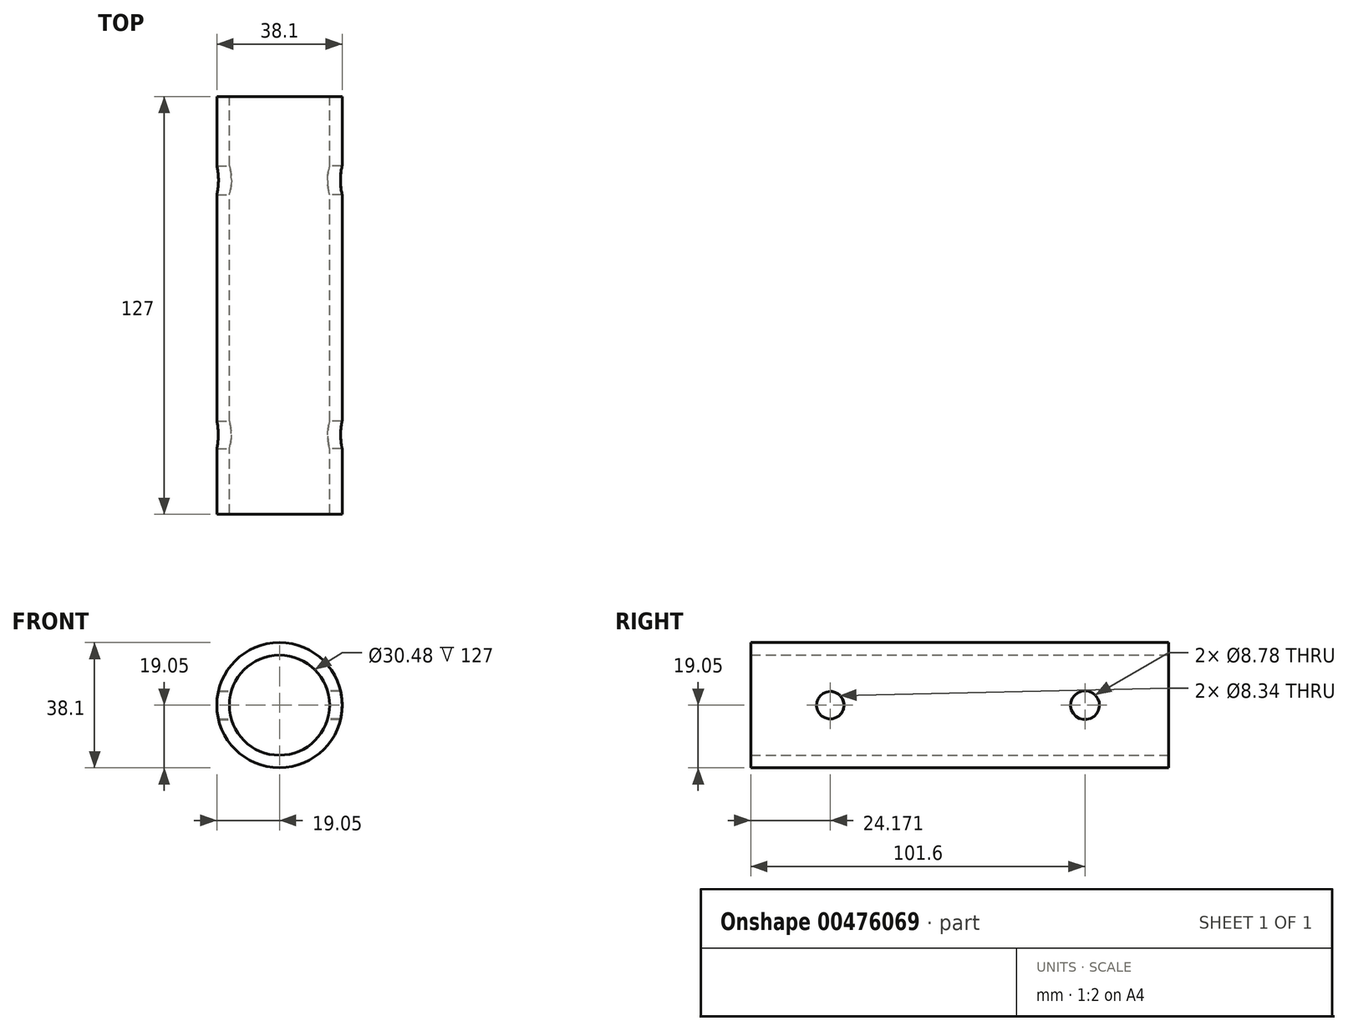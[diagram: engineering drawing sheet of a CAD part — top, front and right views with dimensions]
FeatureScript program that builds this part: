
annotation { "Feature Type Name" : "Feature", "Feature Type Description" : "" }
export const myFeature = defineFeature(function(context is Context, id is Id, definition is map)
    precondition{}
    {
        {
            var Q0;
            Q0=qCreatedBy(makeId("Front.planeOp"),FACE);
            var sketch = newSketch(context, id + "F0", { "sketchPlane" : qUnion([Q0])});
            skCircle(sketch, "E0", {"center": v(0, 0) * mm, "radius": 19.05 * mm});
            skSolve(sketch);
        }
        {
            var Q0;
            Q0=makeQuery(id+"F0.imprint","IMPRINT",FACE,{"disambiguationData":[TD([[makeQuery(id+"F0.imprint","IMPRINT",EDGE,{"derivedFrom":sQuery(id+"F0.wireOp",EDGE,"E0")}),1.0]])]});
            extrude(context, id + "F1", {"entities" : qUnion([Q0]), "depth" : 127 * mm});
        }
        {
            var Q0;
            Q0=makeQuery(id+"F1.opExtrude","CAP_FACE",FACE,{"disambiguationData":[OSD([sQuery(id+"F0.wireOp",EDGE,"E0")])],"isStart":true});
            var sketch = newSketch(context, id + "F2", { "sketchPlane" : qUnion([Q0])});
            skCircle(sketch, "E1", {"center": v(0, 0) * mm, "radius": 15.24 * mm});
            skLineSegment(sketch, "E2", {"start": v(0, -19.05) * mm, "end": v(35.88, -19.05) * mm});
            skSolve(sketch);
        }
        {
            var Q0;
            Q0=makeQuery(id+"F2.imprint","IMPRINT",FACE,{"disambiguationData":[TD([[makeQuery(id+"F2.imprint","IMPRINT",EDGE,{"derivedFrom":sQuery(id+"F2.wireOp",EDGE,"E1")}),1.0]])]});
            extrude(context, id + "F3", {"entities" : qUnion([Q0]), "operationType" : NewBodyOperationType.REMOVE, "oppositeDirection" : true, "depth" : 127 * mm});
        }
        {
            var Q0;
            Q0=qCreatedBy(makeId("Right.planeOp"),FACE);
            var sketch = newSketch(context, id + "F4", { "sketchPlane" : qUnion([Q0])});
            skCircle(sketch, "E3", {"center": v(-102.83, 0) * mm, "radius": 4.17 * mm});
            skCircle(sketch, "E4", {"center": v(-25.4, 0) * mm, "radius": 4.39 * mm});
            skSolve(sketch);
        }
        {
            var Q0;
            Q0 = qSketchRegion(id + "F4", true);
            extrude(context, id + "F5", {"entities" : qUnion([Q0]), "operationType" : NewBodyOperationType.REMOVE, "oppositeDirection" : true, "depth" : 50.8 * mm});
        }
        {
            var Q0;
            Q0 = qSketchRegion(id + "F4", true);
            extrude(context, id + "F6", {"entities" : qUnion([Q0]), "operationType" : NewBodyOperationType.REMOVE, "depth" : 25.4 * mm});
        }
    });
